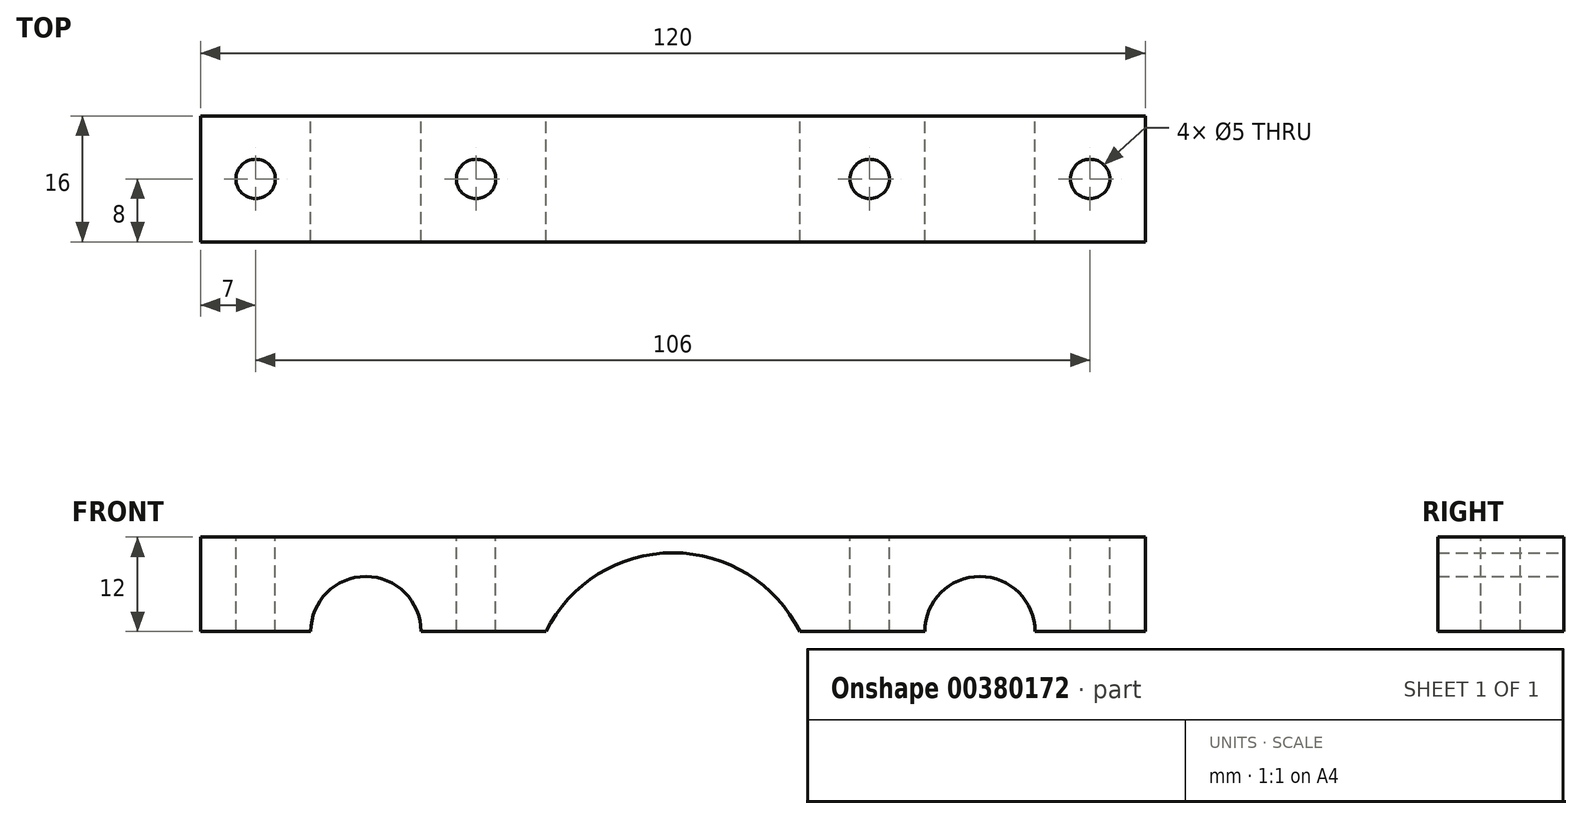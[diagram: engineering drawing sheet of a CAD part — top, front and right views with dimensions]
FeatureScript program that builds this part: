
annotation { "Feature Type Name" : "Feature", "Feature Type Description" : "" }
export const myFeature = defineFeature(function(context is Context, id is Id, definition is map)
    precondition{}
    {
        {
            var Q0;
            Q0=qCreatedBy(makeId("Front.planeOp"),FACE);
            var sketch = newSketch(context, id + "F0", { "sketchPlane" : qUnion([Q0])});
            skLineSegment(sketch, "E0", {"start": v(-46, -6) * mm, "end": v(-60, -6) * mm});
            skLineSegment(sketch, "E1", {"start": v(-60, -6) * mm, "end": v(-60, 6) * mm});
            skLineSegment(sketch, "E2", {"start": v(-60, 6) * mm, "end": v(60, 6) * mm});
            skLineSegment(sketch, "E3", {"start": v(60, 6) * mm, "end": v(60, -6) * mm});
            skLineSegment(sketch, "E4", {"start": v(60, -6) * mm, "end": v(46, -6) * mm});
            skArc(sketch, "E5", {"start": v(46, -6) * mm, "mid": v(39, 1) * mm, "end": v(32, -6) * mm});
            skArc(sketch, "E6", {"start": v(-32, -6) * mm, "mid": v(-39, 1) * mm, "end": v(-46, -6) * mm});
            skArc(sketch, "E7", {"start": v(16.12, -6) * mm, "mid": v(0, 4) * mm, "end": v(-16.12, -6) * mm});
            skLineSegment(sketch, "E8", {"start": v(-32, -6) * mm, "end": v(-16.12, -6) * mm});
            skLineSegment(sketch, "E9", {"start": v(16.12, -6) * mm, "end": v(32, -6) * mm});
            skSolve(sketch);
        }
        {
            var Q0;
            Q0=makeQuery(id+"F0.imprint","IMPRINT",FACE,{"disambiguationData":[TD([[makeQuery(id+"F0.imprint","IMPRINT",EDGE,{"derivedFrom":sQuery(id+"F0.wireOp",EDGE,"E0")}),-1.0]])]});
            extrude(context, id + "F1", {"entities" : qUnion([Q0]), "endBound" : BoundingType.SYMMETRIC, "depth" : 16 * mm});
        }
        {
            var Q0;
            Q0=makeQuery(id+"F1.opExtrude","SWEPT_FACE",FACE,{"disambiguationData":[OSD([sQuery(id+"F0.wireOp",EDGE,"E2")])]});
            var sketch = newSketch(context, id + "F2", { "sketchPlane" : qUnion([Q0])});
            skPoint(sketch, "E10", {"position": v(-53, 0) * mm});
            skPoint(sketch, "E11", {"position": v(-25, 0) * mm});
            skPoint(sketch, "E12", {"position": v(25, 0) * mm});
            skPoint(sketch, "E13", {"position": v(53, 0) * mm});
            skSolve(sketch);
        }
        {
            var Q0;
            Q0=sQuery(id+"F2.wireOp",VERTEX,"E10");
            var Q1;
            Q1=sQuery(id+"F2.wireOp",VERTEX,"E11");
            var Q2;
            Q2=sQuery(id+"F2.wireOp",VERTEX,"E12");
            var Q3;
            Q3=sQuery(id+"F2.wireOp",VERTEX,"E13");
            var Q4;
            Q4=makeQuery(id+"F1.opExtrude","SWEPT_BODY",BODY,{"disambiguationData":[OSD([sQuery(id+"F0.wireOp",EDGE,"E0"),sQuery(id+"F0.wireOp",EDGE,"E1"),sQuery(id+"F0.wireOp",EDGE,"E2"),sQuery(id+"F0.wireOp",EDGE,"E3"),sQuery(id+"F0.wireOp",EDGE,"E4"),sQuery(id+"F0.wireOp",EDGE,"E5"),sQuery(id+"F0.wireOp",EDGE,"E6"),sQuery(id+"F0.wireOp",EDGE,"IZRTLZFC-gH6G-mexX-SaW8-7kCsowfcQd4H")])]});
            hole(context, id + "F3", {"style" : HoleStyle.SIMPLE, "endStyle" : HoleEndStyle.THROUGH, "holeDiameter" : 5 * mm, "isTappedThrough" : true, "tappedDepth" : 12.7 * mm, "tapClearance" : 3, "locations" : qUnion([Q0, Q1, Q2, Q3]), "scope" : qUnion([Q4])});
        }
    });
